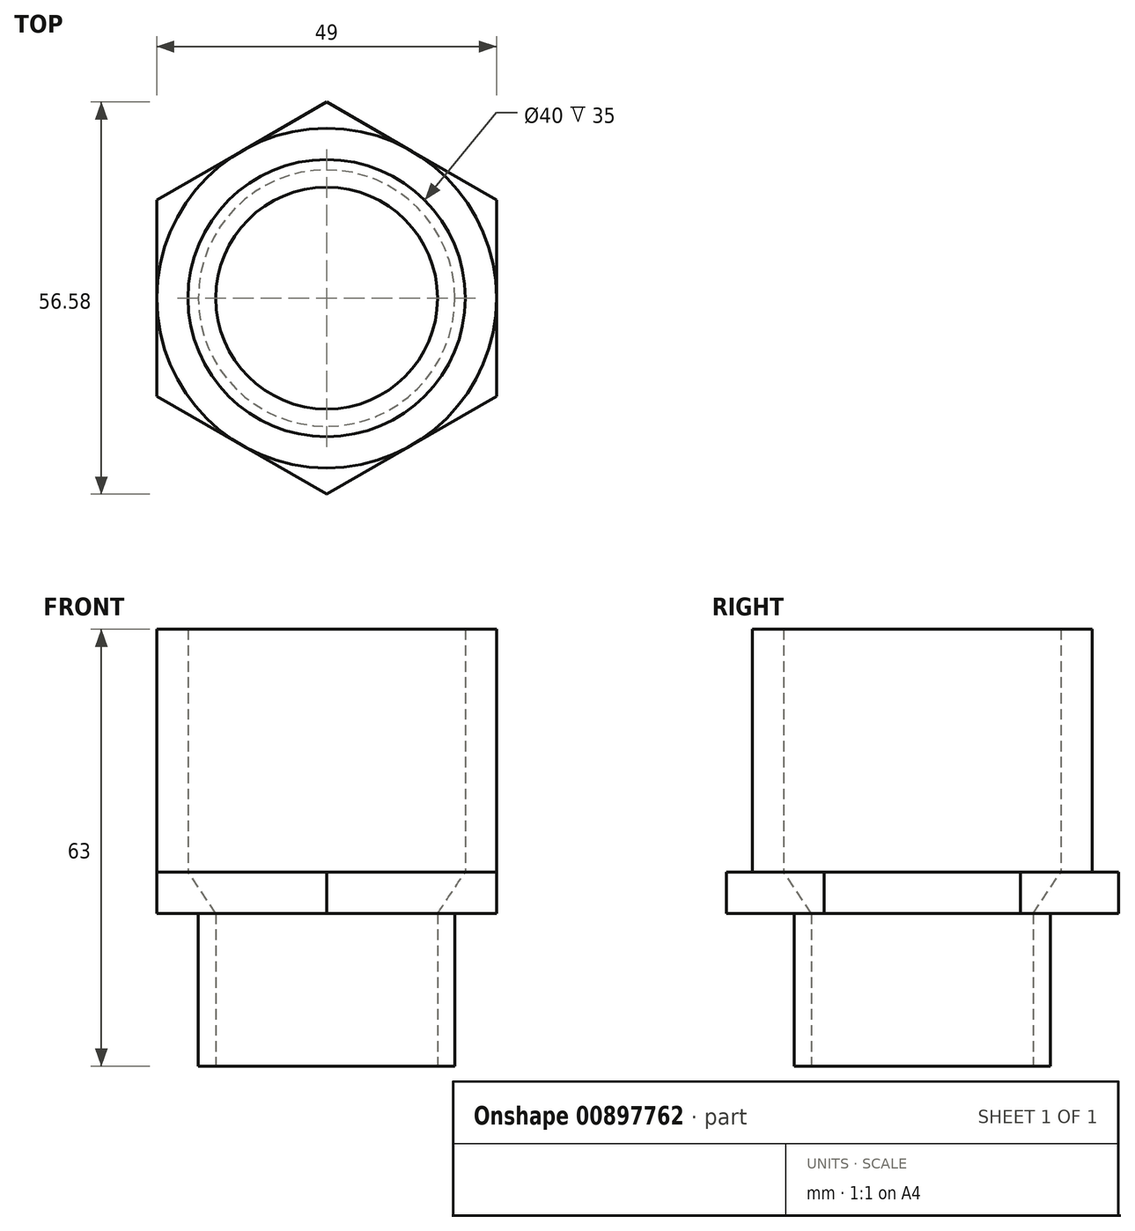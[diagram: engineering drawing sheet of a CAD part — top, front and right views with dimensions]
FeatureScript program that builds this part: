
annotation { "Feature Type Name" : "Feature", "Feature Type Description" : "" }
export const myFeature = defineFeature(function(context is Context, id is Id, definition is map)
    precondition{}
    {
        {
            var Q0;
            Q0=qCreatedBy(makeId("Front.planeOp"),FACE);
            var sketch = newSketch(context, id + "F0", { "sketchPlane" : qUnion([Q0])});
            skLineSegment(sketch, "E0", {"start": v(0, 0) * mm, "end": v(0, 129.6) * mm, "construction": true});
            skLineSegment(sketch, "E1", {"start": v(-16, 0) * mm, "end": v(-18.5, 0) * mm});
            skLineSegment(sketch, "E2", {"start": v(-18.5, 0) * mm, "end": v(-18.5, 22) * mm});
            skLineSegment(sketch, "E3", {"start": v(-18.5, 22) * mm, "end": v(-24.5, 22) * mm});
            skLineSegment(sketch, "E4", {"start": v(-24.5, 22) * mm, "end": v(-24.5, 28) * mm});
            skLineSegment(sketch, "E5", {"start": v(-24.5, 28) * mm, "end": v(-24.5, 63) * mm});
            skLineSegment(sketch, "E6", {"start": v(-24.5, 63) * mm, "end": v(-20, 63) * mm});
            skLineSegment(sketch, "E7", {"start": v(-16, 0) * mm, "end": v(-16, 22) * mm});
            skLineSegment(sketch, "E8", {"start": v(-16, 22) * mm, "end": v(-20, 28) * mm});
            skLineSegment(sketch, "E9", {"start": v(-20, 28) * mm, "end": v(-20, 63) * mm});
            skLineSegment(sketch, "E10", {"start": v(-24.5, 28) * mm, "end": v(-20, 28) * mm, "construction": true});
            skLineSegment(sketch, "E11", {"start": v(-18.5, 22) * mm, "end": v(-16, 22) * mm, "construction": true});
            skSolve(sketch);
        }
        {
            var Q0;
            Q0 = qSketchRegion(id + "F0", true);
            var Q1;
            Q1=sQuery(id+"F0.wireOp",EDGE,"E0");
            revolve(context, id + "F1", {"surfaceOperationType" : NewSurfaceOperationType.NEW, "entities" : qUnion([Q0]), "axis" : qUnion([Q1]), "revolveType" : RevolveType.FULL});
        }
        {
            var Q0;
            Q0=makeQuery(id+"F1.opRevolve","SWEPT_FACE",FACE,{"disambiguationData":[OSD([sQuery(id+"F0.wireOp",EDGE,"E3")])]});
            var sketch = newSketch(context, id + "F2", { "sketchPlane" : qUnion([Q0])});
            skCircle(sketch, "E12.0", {"center": v(0, 0) * mm, "radius": 24.5 * mm});
            skLineSegment(sketch, "E13", {"start": v(-24.5, 14.15) * mm, "end": v(0, 28.3) * mm});
            skLineSegment(sketch, "E14", {"start": v(0, 28.3) * mm, "end": v(24.5, 14.15) * mm});
            skLineSegment(sketch, "E15", {"start": v(24.5, 14.15) * mm, "end": v(24.5, -14.15) * mm});
            skLineSegment(sketch, "E16", {"start": v(24.5, -14.15) * mm, "end": v(0, -28.3) * mm});
            skLineSegment(sketch, "E17", {"start": v(0, -28.3) * mm, "end": v(-24.5, -14.15) * mm});
            skLineSegment(sketch, "E18", {"start": v(-24.5, -14.15) * mm, "end": v(-24.5, 14.15) * mm});
            skCircle(sketch, "E19.0", {"center": v(0, 0) * mm, "radius": 16 * mm});
            skSolve(sketch);
        }
        {
            var Q0;
            Q0 = qSketchRegion(id + "F2", true);
            var Q1;
            Q1=makeQuery(id+"F1.opRevolve","SWEPT_FACE",FACE,{"disambiguationData":[OSD([sQuery(id+"F0.wireOp",EDGE,"E8")])]});
            extrude(context, id + "F3", {"entities" : qUnion([Q0]), "operationType" : NewBodyOperationType.ADD, "oppositeDirection" : true, "depth" : 6 * mm, "endBoundEntityFace" : qUnion([Q1]), "offsetDistance" : 25 * mm});
        }
        {
            var Q0;
            Q0=qCreatedBy(makeId("Front.planeOp"),FACE);
            var sketch = newSketch(context, id + "F4", { "sketchPlane" : qUnion([Q0])});
            skLineSegment(sketch, "E20.0", {"start": v(-16, 22) * mm, "end": v(-20, 28) * mm});
            skLineSegment(sketch, "E20.1.0", {"start": v(-16, 22) * mm, "end": v(0, 22) * mm});
            skLineSegment(sketch, "E20.1.1", {"start": v(0, 22) * mm, "end": v(0, 28) * mm});
            skLineSegment(sketch, "E20.1.2", {"start": v(0, 28) * mm, "end": v(-12.25, 28) * mm});
            skLineSegment(sketch, "E20.1.3", {"start": v(-12.25, 28) * mm, "end": v(-20, 28) * mm});
            skLineSegment(sketch, "E21", {"start": v(0, 28) * mm, "end": v(0, 41.1) * mm, "construction": true});
            skSolve(sketch);
        }
        {
            var Q0;
            Q0 = qSketchRegion(id + "F4", true);
            var Q1;
            Q1=sQuery(id+"F4.wireOp",EDGE,"E21");
            revolve(context, id + "F5", {"operationType" : NewBodyOperationType.REMOVE, "surfaceOperationType" : NewSurfaceOperationType.NEW, "entities" : qUnion([Q0]), "axis" : qUnion([Q1]), "revolveType" : RevolveType.FULL, "oppositeDirection" : true});
        }
    });
